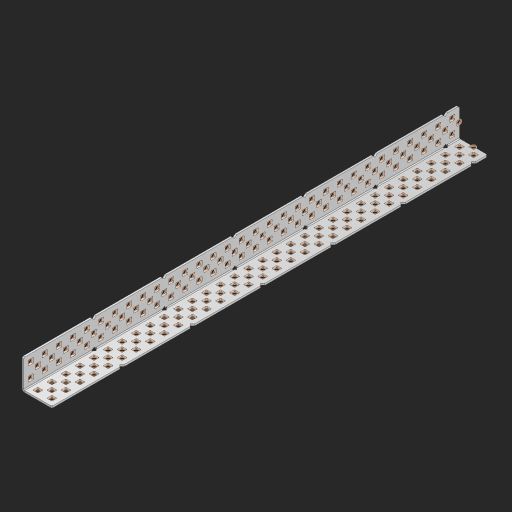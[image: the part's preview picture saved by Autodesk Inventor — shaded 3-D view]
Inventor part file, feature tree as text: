
AUTODESK INVENTOR PART (.ipt)
format: ipt  version: 2023 (Build 270158000, 158)  size: 2,153,984 bytes
history: native  units: in
note: dims shown in document units (in); Inventor stores cm internally (conversion verified against a paired STEP export)
features: other x192, extrude x184, sheet_metal_op x8, sketch x7, pattern_linear x2, mirror x1, chamfer x1
ambient origin geometry x8: Origin, YZ Plane, XZ Plane, XY Plane, X Axis, Y Axis, Z Axis, Center Point
bodies: Solid1 (feature_tree), Body (feature_tree)
feature tree (395):
  sheet_metal_op  "Flanges"
  sheet_metal_op  "Body Pattern"
  pattern_linear  "Center Pattern"  Spacing1=1.0in  [1 undecoded]
  other  "Arc Length"
  pattern_linear  "Notch Pattern"  Spacing1=0.25in  [1 undecoded]
  other  "Diagonal Plane"
  mirror  "Everything Mirrored"
  chamfer  "End Chamfer"
  sketch  "Sketch1"  dims[d0=1.0in]
  other  "Plate1"
  sketch  "Sketch2"  dims[d1=15.5in]
  other  "Plate2"
  sheet_metal_op  "Bend1"
  sheet_metal_op  "Corner1"
  sketch  "Sketch8"  dims[d2=0.0625in]
  sketch  "Sketch9"  dims[d3=0.0625in]
  other  "Srf91"
  sheet_metal_op  "Body Pattern Sketch"
  other  "Srf92"
  sketch  "Sketch13"  dims[d4=0.0312in]
  sketch  "Sketch15"  dims[d5=0.125in]
  sketch  "Sketch16"  dims[d6=0.0625in d7=1.0in d8=90.0deg d9=0.0312in d10=0.25in d11=0.0625in d12=0.0625in d49=0.182in d50=0.02in d52=0.25in d53=0.0625in d54=0.0in d55=0.172in d56=1.0in d57=0.0in d60=12.2047in d62=0.5in d63=0.7874in d65=0.5in d85=0.1473in d86=0.1782in d89=0.0625in d90=0.0in d91=0.04in d92=0.0491in d95=2.5in d96=0.04in d97=0.25in d98=45.0deg d99=0.25in d106=0.182in d107=0.02in d108=0.5in d110=0.0625in d111=0.0in d112=0.172in d113=0.5in d114=0.0in d117=0.5in d123=0.25in d125=0.25in d126=0.0491in d127=0.1473in d128=0.08in d129=0.04in d130=2.5in]
  other  "Srf786"
  other  "Srf856"
  other  "Srf857"
  other  "Srf858"
  other  "Srf859"
  other  "Srf860"
  other  "Srf861"
  other  "Srf889"
  other  "Srf890"
  other  "Srf891"
  other  "Srf1275"
  other  "Srf1276"
  other  "Srf1278"
  other  "Srf1279"
  other  "Srf1280"
  other  "Srf1281"
  other  "Srf1282"
  other  "Srf1283"
  other  "Srf1277"
  other  "Srf1285"
  other  "Srf1286"
  other  "Srf1287"
  other  "Srf1383"
  other  "Srf1384"
  other  "Srf1385"
  other  "Srf1386"
  other  "Srf1387"
  other  "Srf1388"
  other  "Srf1389"
  other  "Srf1390"
  other  "Srf1391"
  other  "Srf1392"
  other  "Srf1393"
  other  "Srf1394"
  other  "Srf1395"
  other  "Srf1396"
  other  "Srf1397"
  other  "Srf1398"
  other  "Srf1399"
  other  "Srf1400"
  other  "Srf1401"
  other  "Srf1402"
  other  "Srf1403"
  other  "Srf1404"
  other  "Srf1405"
  other  "Srf1406"
  other  "Srf1407"
  other  "Srf1408"
  other  "Srf1409"
  other  "Srf1410"
  other  "Srf1411"
  other  "Srf1412"
  other  "Srf1413"
  other  "Srf1414"
  other  "Srf1415"
  other  "Srf1416"
  other  "Srf1417"
  other  "Srf1418"
  other  "Srf1419"
  other  "Srf1420"
  other  "Srf1421"
  other  "Srf1422"
  other  "Srf1423"
  other  "Srf1424"
  other  "Srf1425"
  other  "Srf1426"
  other  "Srf1427"
  other  "Srf1428"
  other  "Srf1429"
  other  "Srf1430"
  other  "Srf1431"
  other  "Srf1432"
  other  "Srf1433"
  other  "Srf1434"
  other  "Srf1435"
  other  "Srf1436"
  other  "Srf1445"
  other  "Srf1446"
  other  "Srf1447"
  other  "Srf1448"
  other  "Srf1449"
  other  "Srf1450"
  other  "Srf1451"
  other  "Srf1452"
  other  "Srf1453"
  other  "Srf1454"
  other  "Srf1455"
  other  "Srf1456"
  other  "Srf1457"
  other  "Srf1458"
  other  "Srf1459"
  other  "Srf1460"
  other  "Srf1461"
  other  "Srf1462"
  other  "Srf1463"
  other  "Srf1464"
  other  "Srf1465"
  other  "Srf1466"
  other  "Srf1467"
  other  "Srf1468"
  other  "Srf1469"
  other  "Srf1470"
  other  "Srf1471"
  other  "Srf1475"
  other  "Srf1476"
  other  "Srf1477"
  other  "Srf1478"
  other  "Srf1479"
  other  "Srf1480"
  other  "Srf1481"
  other  "Srf1482"
  other  "Srf1483"
  other  "Srf1484"
  other  "Srf1485"
  other  "Srf1486"
  other  "Srf1487"
  other  "Srf1488"
  other  "Srf1489"
  other  "Srf1490"
  other  "Srf1491"
  other  "Srf1492"
  other  "Srf1493"
  other  "Srf1494"
  other  "Srf1495"
  other  "Srf1496"
  other  "Srf1497"
  other  "Srf1498"
  other  "Srf1499"
  other  "Srf1500"
  other  "Srf1501"
  other  "Srf1502"
  other  "Srf1503"
  other  "Srf1504"
  other  "Srf1505"
  other  "Srf1506"
  other  "Srf1507"
  other  "Srf1508"
  other  "Srf1509"
  other  "Srf1510"
  other  "Srf1511"
  other  "Srf1512"
  other  "Srf1513"
  other  "Srf1514"
  other  "Srf1515"
  other  "Srf1516"
  other  "Srf1517"
  other  "Srf1518"
  other  "Srf1519"
  other  "Srf1520"
  other  "Srf1521"
  other  "Srf1522"
  other  "Srf1523"
  other  "Srf1524"
  other  "Srf1525"
  other  "Srf1526"
  other  "Srf1527"
  other  "Srf1528"
  other  "Srf1537"
  other  "Srf1538"
  other  "Srf1539"
  other  "Srf1540"
  other  "Srf1541"
  other  "Srf1542"
  other  "Srf1543"
  other  "Srf1544"
  other  "Srf1545"
  other  "Srf1546"
  other  "Srf1547"
  other  "Srf1548"
  other  "Srf1549"
  other  "Srf1550"
  other  "Srf1551"
  other  "Srf1552"
  other  "Srf1553"
  other  "Srf1554"
  other  "Srf1555"
  other  "Srf1556"
  other  "Srf1557"
  other  "Srf1558"
  other  "Srf1559"
  other  "Srf1560"
  other  "Srf1561"
  other  "Srf1562"
  other  "Srf1563"
  sheet_metal_op  "Body Stamp"
  sheet_metal_op  "Body Circle"
  other  "Center Stamp"
  other  "Center Circle"
  sheet_metal_op  "Notch"
  extrude  "ExtrusionSrf92"  Depth=0.0625in
  extrude  "ExtrusionSrf856"  Depth=0.0625in
  extrude  "ExtrusionSrf857"  Depth=0.182in
  extrude  "ExtrusionSrf858"  Depth=0.02in
  extrude  "ExtrusionSrf859"  Depth=0.25in
  extrude  "ExtrusionSrf860"  Depth=0.0625in
  extrude  "ExtrusionSrf861"  TaperAngle=0.0deg  [1 undecoded]
  extrude  "ExtrusionSrf889"  Depth=2.5in
  extrude  "ExtrusionSrf890"  Depth=1.0in TaperAngle=0.0deg
  extrude  "ExtrusionSrf891"  Depth=2.5in
  extrude  "ExtrusionSrf1275"  Depth=0.5in
  extrude  "ExtrusionSrf1276"  Depth=2.5in
  extrude  "ExtrusionSrf1277"  Depth=2.5in
  extrude  "ExtrusionSrf1278"  Depth=0.0625in
  extrude  "ExtrusionSrf1279"  Depth=2.5in TaperAngle=0.0deg
  extrude  "ExtrusionSrf1280"  Depth=2.5in
  extrude  "ExtrusionSrf1281"  Depth=0.25in TaperAngle=45.0deg
  extrude  "ExtrusionSrf1282"  Depth=0.25in
  extrude  "ExtrusionSrf1345"  Depth=0.182in
  extrude  "ExtrusionSrf1346"  Depth=0.02in
  extrude  "ExtrusionSrf1347"  Depth=0.5in
  extrude  "ExtrusionSrf1348"  Depth=0.0625in
  extrude  "ExtrusionSrf1383"  TaperAngle=0.0deg  [1 undecoded]
  extrude  "ExtrusionSrf1384"  Depth=2.5in
  extrude  "ExtrusionSrf1385"  Depth=0.5in TaperAngle=0.0deg
  extrude  "ExtrusionSrf1386"  Depth=0.5in
  extrude  "ExtrusionSrf1387"  Depth=0.25in
  extrude  "ExtrusionSrf1388"  Depth=0.25in
  extrude  "ExtrusionSrf1389"  Depth=2.5in
  extrude  "ExtrusionSrf1390"  Depth=2.5in
  extrude  "ExtrusionSrf1391"  Depth=2.5in
  extrude  "ExtrusionSrf1392"  Depth=2.5in
  extrude  "ExtrusionSrf1393"  Depth=2.5in
  extrude  "ExtrusionSrf1394"  [1 undecoded]
  extrude  "ExtrusionSrf1395"  [1 undecoded]
  extrude  "ExtrusionSrf1396"  [1 undecoded]
  extrude  "ExtrusionSrf1397"  [1 undecoded]
  extrude  "ExtrusionSrf1398"  [1 undecoded]
  extrude  "ExtrusionSrf1399"  [1 undecoded]
  extrude  "ExtrusionSrf1400"  [1 undecoded]
  extrude  "ExtrusionSrf1401"  [1 undecoded]
  extrude  "ExtrusionSrf1402"  [1 undecoded]
  extrude  "ExtrusionSrf1403"  [1 undecoded]
  extrude  "ExtrusionSrf1404"  [1 undecoded]
  extrude  "ExtrusionSrf1405"  [1 undecoded]
  extrude  "ExtrusionSrf1406"  [1 undecoded]
  extrude  "ExtrusionSrf1407"  [1 undecoded]
  extrude  "ExtrusionSrf1408"  [1 undecoded]
  extrude  "ExtrusionSrf1409"  [1 undecoded]
  extrude  "ExtrusionSrf1410"  [1 undecoded]
  extrude  "ExtrusionSrf1411"  [1 undecoded]
  extrude  "ExtrusionSrf1412"  [1 undecoded]
  extrude  "ExtrusionSrf1413"  [1 undecoded]
  extrude  "ExtrusionSrf1414"  [1 undecoded]
  extrude  "ExtrusionSrf1415"  [1 undecoded]
  extrude  "ExtrusionSrf1416"  [1 undecoded]
  extrude  "ExtrusionSrf1417"  [1 undecoded]
  extrude  "ExtrusionSrf1418"  [1 undecoded]
  extrude  "ExtrusionSrf1419"  [1 undecoded]
  extrude  "ExtrusionSrf1420"  [1 undecoded]
  extrude  "ExtrusionSrf1421"  [1 undecoded]
  extrude  "ExtrusionSrf1422"  [1 undecoded]
  extrude  "ExtrusionSrf1423"  [1 undecoded]
  extrude  "ExtrusionSrf1424"  [1 undecoded]
  extrude  "ExtrusionSrf1425"  [1 undecoded]
  extrude  "ExtrusionSrf1426"  [1 undecoded]
  extrude  "ExtrusionSrf1427"  [1 undecoded]
  extrude  "ExtrusionSrf1428"  [1 undecoded]
  extrude  "ExtrusionSrf1429"  [1 undecoded]
  extrude  "ExtrusionSrf1430"  [1 undecoded]
  extrude  "ExtrusionSrf1431"  [1 undecoded]
  extrude  "ExtrusionSrf1432"  [1 undecoded]
  extrude  "ExtrusionSrf1433"  [1 undecoded]
  extrude  "ExtrusionSrf1434"  [1 undecoded]
  extrude  "ExtrusionSrf1435"  [1 undecoded]
  extrude  "ExtrusionSrf1436"  [1 undecoded]
  extrude  "ExtrusionSrf1445"  [1 undecoded]
  extrude  "ExtrusionSrf1446"  [1 undecoded]
  extrude  "ExtrusionSrf1447"  [1 undecoded]
  extrude  "ExtrusionSrf1448"  [1 undecoded]
  extrude  "ExtrusionSrf1449"  [1 undecoded]
  extrude  "ExtrusionSrf1450"  [1 undecoded]
  extrude  "ExtrusionSrf1451"  [1 undecoded]
  extrude  "ExtrusionSrf1452"  [1 undecoded]
  extrude  "ExtrusionSrf1453"  [1 undecoded]
  extrude  "ExtrusionSrf1454"  [1 undecoded]
  extrude  "ExtrusionSrf1455"  [1 undecoded]
  extrude  "ExtrusionSrf1456"  [1 undecoded]
  extrude  "ExtrusionSrf1457"  [1 undecoded]
  extrude  "ExtrusionSrf1458"  [1 undecoded]
  extrude  "ExtrusionSrf1459"  [1 undecoded]
  extrude  "ExtrusionSrf1460"  [1 undecoded]
  extrude  "ExtrusionSrf1461"  [1 undecoded]
  extrude  "ExtrusionSrf1462"  [1 undecoded]
  extrude  "ExtrusionSrf1463"  [1 undecoded]
  extrude  "ExtrusionSrf1464"  [1 undecoded]
  extrude  "ExtrusionSrf1465"  [1 undecoded]
  extrude  "ExtrusionSrf1466"  [1 undecoded]
  extrude  "ExtrusionSrf1467"  [1 undecoded]
  extrude  "ExtrusionSrf1468"  [1 undecoded]
  extrude  "ExtrusionSrf1469"  [1 undecoded]
  extrude  "ExtrusionSrf1470"  [1 undecoded]
  extrude  "ExtrusionSrf1471"  [1 undecoded]
  extrude  "ExtrusionSrf1475"  [1 undecoded]
  extrude  "ExtrusionSrf1476"  [1 undecoded]
  extrude  "ExtrusionSrf1477"  [1 undecoded]
  extrude  "ExtrusionSrf1478"  [1 undecoded]
  extrude  "ExtrusionSrf1479"  [1 undecoded]
  extrude  "ExtrusionSrf1480"  [1 undecoded]
  extrude  "ExtrusionSrf1481"  [1 undecoded]
  extrude  "ExtrusionSrf1482"  [1 undecoded]
  extrude  "ExtrusionSrf1483"  [1 undecoded]
  extrude  "ExtrusionSrf1484"  [1 undecoded]
  extrude  "ExtrusionSrf1485"  [1 undecoded]
  extrude  "ExtrusionSrf1486"  [1 undecoded]
  extrude  "ExtrusionSrf1487"  [1 undecoded]
  extrude  "ExtrusionSrf1488"  [1 undecoded]
  extrude  "ExtrusionSrf1489"  [1 undecoded]
  extrude  "ExtrusionSrf1490"  [1 undecoded]
  extrude  "ExtrusionSrf1491"  [1 undecoded]
  extrude  "ExtrusionSrf1492"  [1 undecoded]
  extrude  "ExtrusionSrf1493"  [1 undecoded]
  extrude  "ExtrusionSrf1494"  [1 undecoded]
  extrude  "ExtrusionSrf1495"  [1 undecoded]
  extrude  "ExtrusionSrf1496"  [1 undecoded]
  extrude  "ExtrusionSrf1497"  [1 undecoded]
  extrude  "ExtrusionSrf1498"  [1 undecoded]
  extrude  "ExtrusionSrf1499"  [1 undecoded]
  extrude  "ExtrusionSrf1500"  [1 undecoded]
  extrude  "ExtrusionSrf1501"  [1 undecoded]
  extrude  "ExtrusionSrf1502"  [1 undecoded]
  extrude  "ExtrusionSrf1503"  [1 undecoded]
  extrude  "ExtrusionSrf1504"  [1 undecoded]
  extrude  "ExtrusionSrf1505"  [1 undecoded]
  extrude  "ExtrusionSrf1506"  [1 undecoded]
  extrude  "ExtrusionSrf1507"  [1 undecoded]
  extrude  "ExtrusionSrf1508"  [1 undecoded]
  extrude  "ExtrusionSrf1509"  [1 undecoded]
  extrude  "ExtrusionSrf1510"  [1 undecoded]
  extrude  "ExtrusionSrf1511"  [1 undecoded]
  extrude  "ExtrusionSrf1512"  [1 undecoded]
  extrude  "ExtrusionSrf1513"  [1 undecoded]
  extrude  "ExtrusionSrf1514"  [1 undecoded]
  extrude  "ExtrusionSrf1515"  [1 undecoded]
  extrude  "ExtrusionSrf1516"  [1 undecoded]
  extrude  "ExtrusionSrf1517"  [1 undecoded]
  extrude  "ExtrusionSrf1518"  [1 undecoded]
  extrude  "ExtrusionSrf1519"  [1 undecoded]
  extrude  "ExtrusionSrf1520"  [1 undecoded]
  extrude  "ExtrusionSrf1521"  [1 undecoded]
  extrude  "ExtrusionSrf1522"  [1 undecoded]
  extrude  "ExtrusionSrf1523"  [1 undecoded]
  extrude  "ExtrusionSrf1524"  [1 undecoded]
  extrude  "ExtrusionSrf1525"  [1 undecoded]
  extrude  "ExtrusionSrf1526"  [1 undecoded]
  extrude  "ExtrusionSrf1527"  [1 undecoded]
  extrude  "ExtrusionSrf1528"  [1 undecoded]
  extrude  "ExtrusionSrf1537"  [1 undecoded]
  extrude  "ExtrusionSrf1538"  [1 undecoded]
  extrude  "ExtrusionSrf1539"  [1 undecoded]
  extrude  "ExtrusionSrf1540"  [1 undecoded]
  extrude  "ExtrusionSrf1541"  [1 undecoded]
  extrude  "ExtrusionSrf1542"  [1 undecoded]
  extrude  "ExtrusionSrf1543"  [1 undecoded]
  extrude  "ExtrusionSrf1544"  [1 undecoded]
  extrude  "ExtrusionSrf1545"  [1 undecoded]
  extrude  "ExtrusionSrf1546"  [1 undecoded]
  extrude  "ExtrusionSrf1547"  [1 undecoded]
  extrude  "ExtrusionSrf1548"  [1 undecoded]
  extrude  "ExtrusionSrf1549"  [1 undecoded]
  extrude  "ExtrusionSrf1550"  [1 undecoded]
  extrude  "ExtrusionSrf1551"  [1 undecoded]
  extrude  "ExtrusionSrf1552"  [1 undecoded]
  extrude  "ExtrusionSrf1553"  [1 undecoded]
  extrude  "ExtrusionSrf1554"  [1 undecoded]
  extrude  "ExtrusionSrf1555"  [1 undecoded]
  extrude  "ExtrusionSrf1556"  [1 undecoded]
  extrude  "ExtrusionSrf1557"  [1 undecoded]
  extrude  "ExtrusionSrf1558"  [1 undecoded]
  extrude  "ExtrusionSrf1559"  [1 undecoded]
  extrude  "ExtrusionSrf1560"  [1 undecoded]
  extrude  "ExtrusionSrf1561"  [1 undecoded]
  extrude  "ExtrusionSrf1562"  [1 undecoded]
  extrude  "ExtrusionSrf1563"  [1 undecoded]
note: 155 required parameter values undecoded (feature->parameter linkage not recoverable at this tier; creation-order binding heuristic only, values carry confidence <= 0.55)
